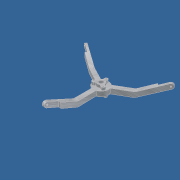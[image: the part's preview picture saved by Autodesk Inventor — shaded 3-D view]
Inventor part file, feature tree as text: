
AUTODESK INVENTOR PART (.ipt)
format: ipt  version: unknown  size: 278,016 bytes
history: native  units: mm
features: sketch x6, extrude x4, sweep x1, pattern_circular x1, projected_geometry x1
ambient origin geometry x8: Origin, YZ Plane, XZ Plane, XY Plane, X Axis, Y Axis, Z Axis, Center Point
feature tree (13):
  extrude  "Выдавливание1"  Depth=4.0mm
  extrude  "Выдавливание2"  Depth=14.2mm
  sweep  "Сдвиг1"
  extrude  "Выдавливание4"  Depth=7.0mm
  pattern_circular  "Круговой массив1"  [2 undecoded]
  extrude  "Выдавливание5"  Depth=5.2mm
  sketch  "Эскиз1"
  sketch  "Эскиз2"
  sketch  "Эскиз4"
  sketch  "Эскиз5"
  projected_geometry  "Спроецированная петля1"
  sketch  "Эскиз6"
  sketch  "Эскиз7"
note: 2 required parameter values undecoded (feature->parameter linkage not recoverable at this tier; creation-order binding heuristic only, values carry confidence <= 0.55)
